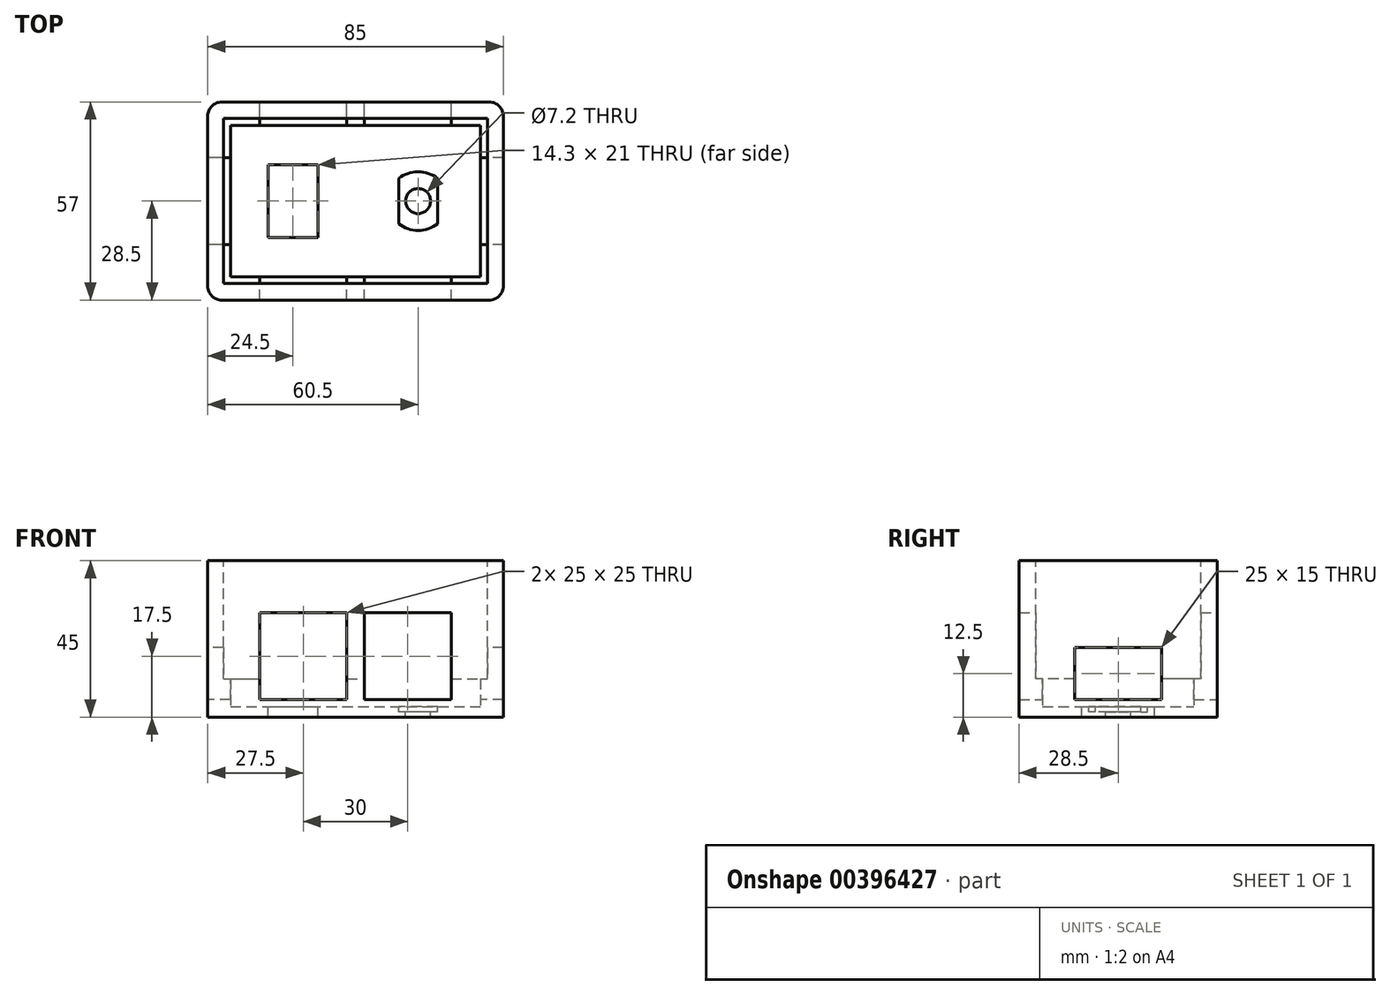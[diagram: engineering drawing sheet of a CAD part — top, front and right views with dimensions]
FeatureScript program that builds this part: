
annotation { "Feature Type Name" : "Feature", "Feature Type Description" : "" }
export const myFeature = defineFeature(function(context is Context, id is Id, definition is map)
    precondition{}
    {
        {
            var Q0;
            Q0=qCreatedBy(makeId("Top.planeOp"),FACE);
            var sketch = newSketch(context, id + "F0", { "sketchPlane" : qUnion([Q0])});
            skLineSegment(sketch, "E0.bottom", {"start": v(-42.5, -28.5) * mm, "end": v(42.5, -28.5) * mm});
            skLineSegment(sketch, "E0.top", {"start": v(-42.5, 28.5) * mm, "end": v(42.5, 28.5) * mm});
            skLineSegment(sketch, "E0.left", {"start": v(-42.5, -28.5) * mm, "end": v(-42.5, 28.5) * mm});
            skLineSegment(sketch, "E0.right", {"start": v(42.5, -28.5) * mm, "end": v(42.5, 28.5) * mm});
            skPoint(sketch, "E0.middle", {"position": v(0, 0) * mm});
            skSolve(sketch);
        }
        {
            var Q0;
            Q0 = qSketchRegion(id + "F0", true);
            extrude(context, id + "F1", {"entities" : qUnion([Q0]), "depth" : 45 * mm});
        }
        {
            var Q0;
            Q0=makeQuery(id+"F1.opExtrude","CAP_FACE",FACE,{"disambiguationData":[OSD([sQuery(id+"F0.wireOp",EDGE,"E0.bottom"),sQuery(id+"F0.wireOp",EDGE,"E0.top"),sQuery(id+"F0.wireOp",EDGE,"E0.left"),sQuery(id+"F0.wireOp",EDGE,"E0.right")])],"isStart":false});
            var sketch = newSketch(context, id + "F2", { "sketchPlane" : qUnion([Q0])});
            skLineSegment(sketch, "E1.bottom", {"start": v(-38, -23.75) * mm, "end": v(38, -23.75) * mm});
            skLineSegment(sketch, "E1.top", {"start": v(-38, 23.75) * mm, "end": v(38, 23.75) * mm});
            skLineSegment(sketch, "E1.left", {"start": v(-38, -23.75) * mm, "end": v(-38, 23.75) * mm});
            skLineSegment(sketch, "E1.right", {"start": v(38, -23.75) * mm, "end": v(38, 23.75) * mm});
            skPoint(sketch, "E1.middle", {"position": v(0, 0) * mm});
            skSolve(sketch);
        }
        {
            var Q0;
            Q0 = qSketchRegion(id + "F2", true);
            extrude(context, id + "F3", {"entities" : qUnion([Q0]), "operationType" : NewBodyOperationType.REMOVE, "oppositeDirection" : true, "depth" : 40 * mm});
        }
        {
            var Q0;
            Q0=makeQuery(id+"F1.opExtrude","SWEPT_EDGE",EDGE,{"disambiguationData":[OSD([sQuery(id+"F0.wireOp",EDGE,"E0.bottom"),sQuery(id+"F0.wireOp",EDGE,"E0.left")])]});
            var Q1;
            Q1=makeQuery(id+"F1.opExtrude","SWEPT_EDGE",EDGE,{"disambiguationData":[OSD([sQuery(id+"F0.wireOp",EDGE,"E0.bottom"),sQuery(id+"F0.wireOp",EDGE,"E0.right")])]});
            var Q2;
            Q2=makeQuery(id+"F1.opExtrude","SWEPT_EDGE",EDGE,{"disambiguationData":[OSD([sQuery(id+"F0.wireOp",EDGE,"E0.top"),sQuery(id+"F0.wireOp",EDGE,"E0.right")])]});
            var Q3;
            Q3=makeQuery(id+"F1.opExtrude","SWEPT_EDGE",EDGE,{"disambiguationData":[OSD([sQuery(id+"F0.wireOp",EDGE,"E0.top"),sQuery(id+"F0.wireOp",EDGE,"E0.left")])]});
            fillet(context, id + "F4", {"entities" : qUnion([Q0, Q1, Q2, Q3]), "radius" : 4 * mm, "tangentPropagation" : true, "allowEdgeOverflow" : false});
        }
        {
            var Q0;
            Q0=qCreatedBy(makeId("Top.planeOp"),FACE);
            var sketch = newSketch(context, id + "F5", { "sketchPlane" : qUnion([Q0])});
            skLineSegment(sketch, "E2.bottom", {"start": v(-38.5, -28.5) * mm, "end": v(38.5, -28.5) * mm});
            skLineSegment(sketch, "E2.top", {"start": v(-38.5, 28.5) * mm, "end": v(38.5, 28.5) * mm});
            skLineSegment(sketch, "E2.left", {"start": v(-42.5, -24.5) * mm, "end": v(-42.5, 24.5) * mm});
            skLineSegment(sketch, "E2.right", {"start": v(42.5, -24.5) * mm, "end": v(42.5, 24.5) * mm});
            skPoint(sketch, "E2.middle", {"position": v(0, 0) * mm});
            skPoint(sketch, "E3.visualSharp", {"position": v(-42.5, 28.5) * mm});
            skArc(sketch, "E3.filletArc", {"start": v(-38.5, 28.5) * mm, "mid": v(-41.33, 27.33) * mm, "end": v(-42.5, 24.5) * mm});
            skPoint(sketch, "E4.visualSharp", {"position": v(42.5, 28.5) * mm});
            skArc(sketch, "E4.filletArc", {"start": v(42.5, 24.5) * mm, "mid": v(41.33, 27.33) * mm, "end": v(38.5, 28.5) * mm});
            skPoint(sketch, "E5.visualSharp", {"position": v(42.5, -28.5) * mm});
            skArc(sketch, "E5.filletArc", {"start": v(38.5, -28.5) * mm, "mid": v(41.33, -27.33) * mm, "end": v(42.5, -24.5) * mm});
            skPoint(sketch, "E6.visualSharp", {"position": v(-42.5, -28.5) * mm});
            skArc(sketch, "E6.filletArc", {"start": v(-42.5, -24.5) * mm, "mid": v(-41.33, -27.33) * mm, "end": v(-38.5, -28.5) * mm});
            skSolve(sketch);
        }
        {
            var Q0;
            Q0 = qSketchRegion(id + "F5", true);
            extrude(context, id + "F6", {"entities" : qUnion([Q0]), "depth" : 6 * mm});
        }
        {
            var Q0;
            Q0=makeQuery(id+"F6.opExtrude","CAP_FACE",FACE,{"disambiguationData":[OSD([sQuery(id+"F5.wireOp",EDGE,"E2.bottom"),sQuery(id+"F5.wireOp",EDGE,"E2.top"),sQuery(id+"F5.wireOp",EDGE,"E2.left"),sQuery(id+"F5.wireOp",EDGE,"E2.right"),sQuery(id+"F5.wireOp",EDGE,"E3.filletArc"),sQuery(id+"F5.wireOp",EDGE,"E4.filletArc"),sQuery(id+"F5.wireOp",EDGE,"E5.filletArc"),sQuery(id+"F5.wireOp",EDGE,"E6.filletArc")])],"isStart":false});
            var sketch = newSketch(context, id + "F7", { "sketchPlane" : qUnion([Q0])});
            skPoint(sketch, "E7.endSnap0", {"position": v(0, 28.5) * mm});
            skPoint(sketch, "E8.endSnap0", {"position": v(0, -28.5) * mm});
            skPoint(sketch, "E9.endSnap0", {"position": v(-42.5, 0) * mm});
            skPoint(sketch, "E10.endSnap0", {"position": v(42.5, 0) * mm});
            skLineSegment(sketch, "E11.bottom", {"start": v(-38, -23.75) * mm, "end": v(38, -23.75) * mm});
            skLineSegment(sketch, "E11.top", {"start": v(-38, 23.75) * mm, "end": v(38, 23.75) * mm});
            skLineSegment(sketch, "E11.left", {"start": v(-38, -23.75) * mm, "end": v(-38, 23.75) * mm});
            skPoint(sketch, "E11.middle", {"position": v(0, 0) * mm});
            skPoint(sketch, "E9.end.orphan", {"position": v(-38, 0) * mm});
            skLineSegment(sketch, "E12", {"start": v(38, 23.75) * mm, "end": v(38, -23.75) * mm});
            skPoint(sketch, "E7.end.orphan", {"position": v(0, 23.75) * mm});
            skPoint(sketch, "E7.start.orphan", {"position": v(0, 28.5) * mm});
            skPoint(sketch, "E8.end.orphan", {"position": v(0, -23.75) * mm});
            skPoint(sketch, "E8.start.orphan", {"position": v(0, -28.5) * mm});
            skLineSegment(sketch, "E13.0", {"start": v(-36, 21.75) * mm, "end": v(36, 21.75) * mm});
            skLineSegment(sketch, "E13.1", {"start": v(-36, -21.75) * mm, "end": v(-36, 21.75) * mm});
            skLineSegment(sketch, "E13.2", {"start": v(-36, -21.75) * mm, "end": v(36, -21.75) * mm});
            skLineSegment(sketch, "E13.3", {"start": v(36, 21.75) * mm, "end": v(36, -21.75) * mm});
            skSolve(sketch);
        }
        {
            var Q0;
            Q0 = qSketchRegion(id + "F7", true);
            extrude(context, id + "F8", {"entities" : qUnion([Q0]), "operationType" : NewBodyOperationType.ADD, "depth" : 5 * mm});
        }
        {
            var Q0;
            Q0=makeQuery(id+"F8.boolean.opBoolean","SPLIT",FACE,{"disambiguationData":[TD([makeQuery(id+"F8.opExtrude","SWEPT_FACE",FACE,{"disambiguationData":[OSD([sQuery(id+"F7.wireOp",EDGE,"E13.0")])]})])],"derivedFrom":makeQuery(id+"F6.opExtrude","CAP_FACE",FACE,{"disambiguationData":[OSD([sQuery(id+"F5.wireOp",EDGE,"E2.bottom"),sQuery(id+"F5.wireOp",EDGE,"E2.top"),sQuery(id+"F5.wireOp",EDGE,"E2.left"),sQuery(id+"F5.wireOp",EDGE,"E2.right"),sQuery(id+"F5.wireOp",EDGE,"E3.filletArc"),sQuery(id+"F5.wireOp",EDGE,"E4.filletArc"),sQuery(id+"F5.wireOp",EDGE,"E5.filletArc"),sQuery(id+"F5.wireOp",EDGE,"E6.filletArc")])],"isStart":false})});
            var sketch = newSketch(context, id + "F9", { "sketchPlane" : qUnion([Q0])});
            skLineSegment(sketch, "E14.bottom", {"start": v(-36, -21.75) * mm, "end": v(36, -21.75) * mm});
            skLineSegment(sketch, "E14.top", {"start": v(-36, 21.75) * mm, "end": v(36, 21.75) * mm});
            skLineSegment(sketch, "E14.left", {"start": v(-36, -21.75) * mm, "end": v(-36, 21.75) * mm});
            skLineSegment(sketch, "E14.right", {"start": v(36, -21.75) * mm, "end": v(36, 21.75) * mm});
            skPoint(sketch, "E14.middle", {"position": v(0, 0) * mm});
            skSolve(sketch);
        }
        {
            var Q0;
            Q0 = qSketchRegion(id + "F9", true);
            extrude(context, id + "F10", {"entities" : qUnion([Q0]), "operationType" : NewBodyOperationType.REMOVE, "oppositeDirection" : true, "depth" : 3 * mm});
        }
        {
            var Q0;
            Q0=makeQuery(id+"F10.boolean.opBoolean","COPY",FACE,{"derivedFrom":makeQuery(id+"F10.opExtrude","CAP_FACE",FACE,{"disambiguationData":[OSD([sQuery(id+"F9.wireOp",EDGE,"E14.bottom"),sQuery(id+"F9.wireOp",EDGE,"E14.top"),sQuery(id+"F9.wireOp",EDGE,"E14.left"),sQuery(id+"F9.wireOp",EDGE,"E14.right")])],"isStart":false})});
            var sketch = newSketch(context, id + "F11", { "sketchPlane" : qUnion([Q0])});
            skPoint(sketch, "E15.end.orphan", {"position": v(-36, 0) * mm});
            skLineSegment(sketch, "E16.bottom", {"start": v(-25.15, -10.5) * mm, "end": v(-10.85, -10.5) * mm});
            skLineSegment(sketch, "E16.top", {"start": v(-25.15, 10.5) * mm, "end": v(-10.85, 10.5) * mm});
            skLineSegment(sketch, "E16.left", {"start": v(-25.15, -10.5) * mm, "end": v(-25.15, 10.5) * mm});
            skLineSegment(sketch, "E16.right", {"start": v(-10.85, -10.5) * mm, "end": v(-10.85, 10.5) * mm});
            skPoint(sketch, "E16.middle", {"position": v(-18, 0) * mm});
            skPoint(sketch, "E17.endSnap0", {"position": v(36, 0) * mm});
            skCircle(sketch, "E18", {"center": v(18, 0) * mm, "radius": 3.6 * mm});
            skPoint(sketch, "E17.start.orphan", {"position": v(36, 0) * mm});
            skSolve(sketch);
        }
        {
            var Q0;
            Q0 = qSketchRegion(id + "F11", true);
            extrude(context, id + "F12", {"entities" : qUnion([Q0]), "operationType" : NewBodyOperationType.REMOVE, "oppositeDirection" : true, "depth" : 25 * mm});
        }
        {
            var Q0;
            Q0=makeQuery(id+"F1.opExtrude","SWEPT_FACE",FACE,{"disambiguationData":[OSD([sQuery(id+"F0.wireOp",EDGE,"E0.left")])]});
            var sketch = newSketch(context, id + "F13", { "sketchPlane" : qUnion([Q0])});
            skLineSegment(sketch, "E19", {"start": v(0, 5) * mm, "end": v(-12.5, 5) * mm});
            skLineSegment(sketch, "E20", {"start": v(-12.5, 5) * mm, "end": v(12.5, 5) * mm});
            skLineSegment(sketch, "E21", {"start": v(-12.5, 5) * mm, "end": v(-12.5, 20) * mm});
            skLineSegment(sketch, "E22", {"start": v(12.5, 20) * mm, "end": v(-12.5, 20) * mm});
            skLineSegment(sketch, "E23", {"start": v(12.5, 5) * mm, "end": v(12.5, 20) * mm});
            skPoint(sketch, "E24.start.orphan", {"position": v(0, 0) * mm});
            skSolve(sketch);
        }
        {
            var Q0;
            Q0 = qSketchRegion(id + "F13", true);
            extrude(context, id + "F14", {"entities" : qUnion([Q0]), "operationType" : NewBodyOperationType.REMOVE, "endBound" : BoundingType.THROUGH_ALL, "oppositeDirection" : true, "depth" : 82 * mm});
        }
        {
            var Q0;
            Q0=makeQuery(id+"F1.opExtrude","SWEPT_FACE",FACE,{"disambiguationData":[OSD([sQuery(id+"F0.wireOp",EDGE,"E0.top")])]});
            var sketch = newSketch(context, id + "F15", { "sketchPlane" : qUnion([Q0])});
            skPoint(sketch, "E25.end.orphan", {"position": v(-27.5, 5) * mm});
            skPoint(sketch, "E25.start.orphan", {"position": v(-38.5, 5) * mm});
            skLineSegment(sketch, "E26", {"start": v(-27.5, 5) * mm, "end": v(-2.5, 5) * mm});
            skLineSegment(sketch, "E27", {"start": v(-27.5, 5) * mm, "end": v(-27.5, 30) * mm});
            skLineSegment(sketch, "E28", {"start": v(27.5, 5) * mm, "end": v(27.5, 30) * mm});
            skLineSegment(sketch, "E29", {"start": v(27.5, 30) * mm, "end": v(2.5, 30) * mm});
            skPoint(sketch, "E30.endSnap0", {"position": v(0, 5) * mm});
            skPoint(sketch, "E30.endSnap1", {"position": v(-27.5, 17.5) * mm});
            skPoint(sketch, "E30.end.orphan", {"position": v(0, 17.5) * mm});
            skPoint(sketch, "E30.start.orphan", {"position": v(-27.5, 17.5) * mm});
            skLineSegment(sketch, "E31.left", {"start": v(-2.5, 5) * mm, "end": v(-2.5, 30) * mm});
            skLineSegment(sketch, "E31.right", {"start": v(2.5, 5) * mm, "end": v(2.5, 30) * mm});
            skLineSegment(sketch, "E32.trimOffspring", {"start": v(2.5, 5) * mm, "end": v(27.5, 5) * mm});
            skLineSegment(sketch, "E33.trimOffspring", {"start": v(-2.5, 30) * mm, "end": v(-27.5, 30) * mm});
            skSolve(sketch);
        }
        {
            var Q0;
            Q0 = qSketchRegion(id + "F15", true);
            extrude(context, id + "F16", {"entities" : qUnion([Q0]), "operationType" : NewBodyOperationType.REMOVE, "endBound" : BoundingType.THROUGH_ALL, "oppositeDirection" : true, "depth" : 25 * mm});
        }
        {
            var Q0;
            Q0=makeQuery(id+"F10.boolean.opBoolean","COPY",FACE,{"derivedFrom":makeQuery(id+"F10.opExtrude","CAP_FACE",FACE,{"disambiguationData":[OSD([sQuery(id+"F9.wireOp",EDGE,"E14.bottom"),sQuery(id+"F9.wireOp",EDGE,"E14.top"),sQuery(id+"F9.wireOp",EDGE,"E14.left"),sQuery(id+"F9.wireOp",EDGE,"E14.right")])],"isStart":false})});
            var sketch = newSketch(context, id + "F17", { "sketchPlane" : qUnion([Q0])});
            skLineSegment(sketch, "E34", {"start": v(12.4, 6.51) * mm, "end": v(12.4, -6.51) * mm});
            skLineSegment(sketch, "E35", {"start": v(23.6, 6.51) * mm, "end": v(23.6, -6.51) * mm});
            skPoint(sketch, "E36.center.orphan", {"position": v(18, 0) * mm});
            skLineSegment(sketch, "E37", {"start": v(18, 0) * mm, "end": v(18, 0) * mm});
            skPoint(sketch, "E38.orphan", {"position": v(12.4, 0) * mm});
            skPoint(sketch, "E39.end.orphan", {"position": v(23.6, 0) * mm});
            skPoint(sketch, "E40.end.orphan", {"position": v(10.47, 6.94) * mm});
            skPoint(sketch, "E40.start.orphan", {"position": v(18, 7.15) * mm});
            skPoint(sketch, "E41.end.orphan", {"position": v(10.6, -6.94) * mm});
            skPoint(sketch, "E41.start.orphan", {"position": v(18, -7.15) * mm});
            skArc(sketch, "E42", {"start": v(23.6, 6.51) * mm, "mid": v(18, 8.47) * mm, "end": v(12.4, 6.51) * mm});
            skArc(sketch, "E43", {"start": v(12.4, -6.51) * mm, "mid": v(18, -8.47) * mm, "end": v(23.6, -6.51) * mm});
            skSolve(sketch);
        }
        {
            var Q0;
            Q0 = qSketchRegion(id + "F17", true);
            extrude(context, id + "F18", {"entities" : qUnion([Q0]), "operationType" : NewBodyOperationType.REMOVE, "oppositeDirection" : true, "depth" : 1.5 * mm});
        }
        {
            var Q0;
            Q0 = qSketchRegion(id + "F17", true);
            extrude(context, id + "F19", {"entities" : qUnion([Q0]), "operationType" : NewBodyOperationType.REMOVE, "oppositeDirection" : true, "depth" : 1.5 * mm});
        }
    });
